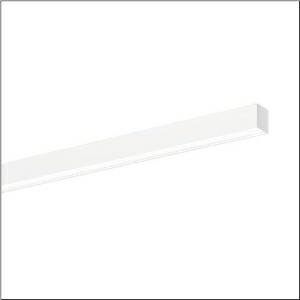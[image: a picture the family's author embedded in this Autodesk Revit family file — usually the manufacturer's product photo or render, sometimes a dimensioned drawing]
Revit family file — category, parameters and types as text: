
# Revit family: silica_21_51mx23db35wb
name_source: partatom
category: Lighting Fixtures
units: mm (PartAtom-declared; Revit-internal decimal feet)

## family parameters
Cut with Voids When Loaded = No
Host = Face
Light Source = No
Part Type = Normal
Room Calculation Point = No
Round Connector Dimension = Use Diameter
Shared = No

## types (1)
- --- (1 x LED, 4100 lm, 30.1 W, 3000K)
    Apparent Load = 30 VA
    CIE Flux Codes = 78 96 99 100 100
    Color Rendering = 80
    Color Temperature = 3000K
    Default Elevation = 1800 mm
    Description = Silica 21, office luminaire, primary optical cover: prismatic diffuser, of PMMA, CAT 2 (L<= 3000cd/m²), light emission: direct distribution, primary light characteristic: symmetric, installation type: surface-mounted, LED, rated luminous flux: 4.100lm, luminous efficacy: 136lm/W, light colour: 830, colour temperature: 3000K, control gear: DALI 2, with terminal, 3+2-pole, max. 2.5mm², mains connection: 220..240V, AC, 50/60Hz, rated input power: 30.1W, luminaire housing, of aluminium, traffic white (RAL 9016), length: 1.504mm, width: 53mm, height: 53mm, protection rating (complete): IP20, insulation class (complete): insulation class I (protective earthing), certification: CE, permissible operating ambient temperature: 0..+35°C, standard: EN 50419, packaging unit: 1 piece
    Height = 53 mm
    Lamp = 1 x LED
    Lamp Light Flux = 4100 lm
    Lamp Power = 30.1 W
    Lamp count = 1
    Length = 1504 mm
    Luminous efficacy = 136 lm/W
    Manufacturer = Siteco
    ModVariant = No
    Model = 51MX23DB35WB
    Mounting Place = Ceiling
    Mounting Type = Surface mounted
    Number of Poles = 1
    OnlyDefault = Yes
    Power Factor = 1
    Product Name = Silica 21
    Product group = office luminaire | ceiling mounted
    ProductGroupID = 301
    Protection Class = Protection class I
    Protection Degree = IP 20
    RLX_Detail_Level = 1
    RLX_Emergency_Light_Flux = 0 lm
    RLX_Emergency_Type = 0
    RLX_Emergency_Type_DB = No
    RlxData = <blob elided: 18805 chars, md5=e996de6a>
    Socket = socket
    Standby Power = 0 W
    System Light Flux = 4100 lm
    System Power = 30 W
    Type Comments = factory setting: luminous flux: 100 % | dim-lin: 254 | 345 mA
    Type Image = l_1335877.jpg
    URL = http://relux.com
    VarID = @adj_119715
    Voltage = 0 V
    Weight = 0.00 kg
    Width = 53 mm

## geometry (parser evidence)
native form markers: Blend x4, Sweep x10
no freeform markers — native parametric forms only
